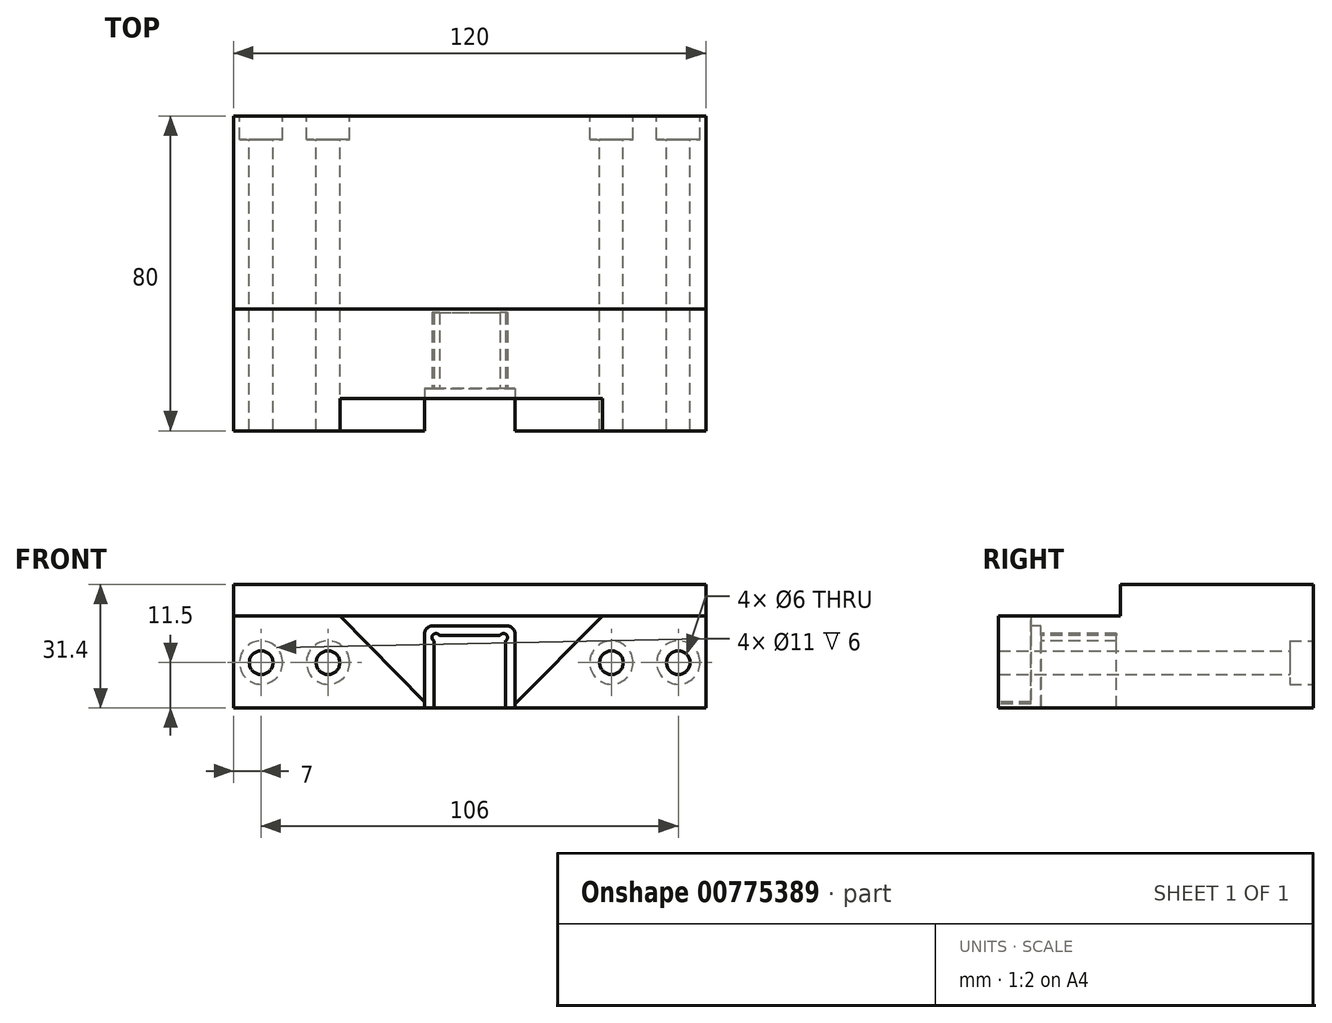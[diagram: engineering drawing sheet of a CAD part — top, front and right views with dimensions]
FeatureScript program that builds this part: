
annotation { "Feature Type Name" : "Feature", "Feature Type Description" : "" }
export const myFeature = defineFeature(function(context is Context, id is Id, definition is map)
    precondition{}
    {
        {
            var Q0;
            Q0=qCreatedBy(makeId("Front.planeOp"),FACE);
            var sketch = newSketch(context, id + "F0", { "sketchPlane" : qUnion([Q0])});
            skLineSegment(sketch, "E0.bottom", {"start": v(-60, 0) * mm, "end": v(60, 0) * mm});
            skLineSegment(sketch, "E0.top", {"start": v(-60, -39.79) * mm, "end": v(60, -39.79) * mm});
            skLineSegment(sketch, "E0.left", {"start": v(-60, 0) * mm, "end": v(-60, -39.79) * mm});
            skLineSegment(sketch, "E0.right", {"start": v(60, 0) * mm, "end": v(60, -39.79) * mm});
            skSolve(sketch);
        }
        {
            var Q0;
            Q0 = qSketchRegion(id + "F0", true);
            extrude(context, id + "F1", {"entities" : qUnion([Q0]), "depth" : 80 * mm, "offsetDistance" : 25 * mm});
        }
        {
            var Q0;
            Q0=makeQuery(id+"F1.opExtrude","CAP_FACE",FACE,{"disambiguationData":[OSD([sQuery(id+"F0.wireOp",EDGE,"E0.bottom"),sQuery(id+"F0.wireOp",EDGE,"E0.top"),sQuery(id+"F0.wireOp",EDGE,"E0.left"),sQuery(id+"F0.wireOp",EDGE,"E0.right")])],"isStart":false});
            var sketch = newSketch(context, id + "F2", { "sketchPlane" : qUnion([Q0])});
            skLineSegment(sketch, "E1.bottom", {"start": v(-9.09, -39.79) * mm, "end": v(9.09, -39.79) * mm});
            skLineSegment(sketch, "E1.top", {"start": v(-9.1, -21.39) * mm, "end": v(9.1, -21.39) * mm});
            skLineSegment(sketch, "E1.left", {"start": v(-9.09, -39.79) * mm, "end": v(-9.1, -21.39) * mm});
            skLineSegment(sketch, "E1.right", {"start": v(9.1, -39.79) * mm, "end": v(9.1, -21.39) * mm});
            skSolve(sketch);
        }
        {
            var Q0;
            Q0 = qSketchRegion(id + "F2", true);
            extrude(context, id + "F3", {"entities" : qUnion([Q0]), "operationType" : NewBodyOperationType.REMOVE, "oppositeDirection" : true, "depth" : 30.03 * mm, "offsetDistance" : 25 * mm});
        }
        {
            var Q0;
            Q0=makeQuery(id+"F1.opExtrude","CAP_FACE",FACE,{"disambiguationData":[OSD([sQuery(id+"F0.wireOp",EDGE,"E0.bottom"),sQuery(id+"F0.wireOp",EDGE,"E0.top"),sQuery(id+"F0.wireOp",EDGE,"E0.left"),sQuery(id+"F0.wireOp",EDGE,"E0.right")])],"isStart":false});
            var sketch = newSketch(context, id + "F4", { "sketchPlane" : qUnion([Q0])});
            skLineSegment(sketch, "E2.bottom", {"start": v(-11.5, -39.79) * mm, "end": v(11.5, -39.79) * mm});
            skLineSegment(sketch, "E2.top", {"start": v(-11.5, -18.99) * mm, "end": v(11.5, -18.99) * mm});
            skLineSegment(sketch, "E2.left", {"start": v(-11.5, -39.79) * mm, "end": v(-11.5, -18.99) * mm});
            skLineSegment(sketch, "E2.right", {"start": v(11.5, -39.79) * mm, "end": v(11.5, -18.99) * mm});
            skSolve(sketch);
        }
        {
            var Q0;
            Q0 = qSketchRegion(id + "F4", true);
            extrude(context, id + "F5", {"entities" : qUnion([Q0]), "operationType" : NewBodyOperationType.REMOVE, "oppositeDirection" : true, "depth" : 10.8 * mm, "offsetDistance" : 25 * mm});
        }
        {
            var Q0;
            Q0=makeQuery(id+"F5.boolean.opBoolean","COPY",FACE,{"derivedFrom":makeQuery(id+"F5.opExtrude","CAP_FACE",FACE,{"disambiguationData":[OSD([sQuery(id+"F4.wireOp",EDGE,"E2.bottom"),sQuery(id+"F4.wireOp",EDGE,"E2.top"),sQuery(id+"F4.wireOp",EDGE,"E2.left"),sQuery(id+"F4.wireOp",EDGE,"E2.right")])],"isStart":false})});
            var sketch = newSketch(context, id + "F6", { "sketchPlane" : qUnion([Q0])});
            skLineSegment(sketch, "E3.0", {"start": v(-9.6, -20.89) * mm, "end": v(-9.59, -39.79) * mm});
            skLineSegment(sketch, "E3.1", {"start": v(9.6, -20.89) * mm, "end": v(-9.6, -20.89) * mm});
            skLineSegment(sketch, "E3.2", {"start": v(9.6, -20.89) * mm, "end": v(9.6, -39.79) * mm});
            skCircle(sketch, "E4", {"center": v(-8.6, -21.89) * mm, "radius": 1 * mm});
            skCircle(sketch, "E5", {"center": v(8.59, -21.89) * mm, "radius": 1 * mm});
            skSolve(sketch);
        }
        {
            var Q0;
            {var subQ0=sQuery(id+"F6.wireOp",EDGE,"E4");var subQ1=makeQuery(id+"F6.imprint","INTERSECT",VERTEX,{"derivedFrom":[sQuery(id+"F6.wireOp",EDGE,"E3.0"),subQ0]});Q0=makeQuery(id+"F6.imprint","IMPRINT",FACE,{"disambiguationData":[TD([[makeQuery(id+"F6.imprint","IMPRINT",EDGE,{"disambiguationData":[TD([[subQ1,1.0]])],"derivedFrom":subQ0}),1.0]])]});}
            var Q1;
            {var subQ4=sQuery(id+"F6.wireOp",EDGE,"E5");var subQ8=makeQuery(id+"F6.imprint","INTERSECT",VERTEX,{"derivedFrom":[sQuery(id+"F6.wireOp",EDGE,"E3.1"),subQ4]});Q1=makeQuery(id+"F6.imprint","IMPRINT",FACE,{"disambiguationData":[TD([[makeQuery(id+"F6.imprint","IMPRINT",EDGE,{"disambiguationData":[TD([[subQ8,1.0]])],"derivedFrom":subQ4}),1.0]])]});}
            var Q2;
            Q2=makeQuery(id+"F3.boolean.opBoolean","COPY",FACE,{"derivedFrom":makeQuery(id+"F3.opExtrude","CAP_FACE",FACE,{"disambiguationData":[OSD([sQuery(id+"F2.wireOp",EDGE,"E1.bottom"),sQuery(id+"F2.wireOp",EDGE,"E1.top"),sQuery(id+"F2.wireOp",EDGE,"E1.left"),sQuery(id+"F2.wireOp",EDGE,"E1.right")])],"isStart":false})});
            extrude(context, id + "F7", {"entities" : qUnion([Q0, Q1]), "operationType" : NewBodyOperationType.REMOVE, "endBound" : BoundingType.UP_TO_SURFACE, "oppositeDirection" : true, "depth" : 25 * mm, "endBoundEntityFace" : qUnion([Q2]), "offsetDistance" : 25 * mm});
        }
        {
            var Q0;
            Q0=makeQuery(id+"F5.boolean.opBoolean","COPY",EDGE,{"derivedFrom":makeQuery(id+"F5.opExtrude","SWEPT_EDGE",EDGE,{"disambiguationData":[OSD([sQuery(id+"F4.wireOp",EDGE,"E2.top"),sQuery(id+"F4.wireOp",EDGE,"E2.left")])]})});
            var Q1;
            Q1=makeQuery(id+"F5.boolean.opBoolean","COPY",EDGE,{"derivedFrom":makeQuery(id+"F5.opExtrude","SWEPT_EDGE",EDGE,{"disambiguationData":[OSD([sQuery(id+"F4.wireOp",EDGE,"E2.top"),sQuery(id+"F4.wireOp",EDGE,"E2.right")])]})});
            fillet(context, id + "F8", {"entities" : qUnion([Q0, Q1]), "radius" : 2 * mm, "tangentPropagation" : true, "allowEdgeOverflow" : false});
        }
        {
            var Q0;
            Q0=makeQuery(id+"F1.opExtrude","CAP_FACE",FACE,{"disambiguationData":[OSD([sQuery(id+"F0.wireOp",EDGE,"E0.bottom"),sQuery(id+"F0.wireOp",EDGE,"E0.top"),sQuery(id+"F0.wireOp",EDGE,"E0.left"),sQuery(id+"F0.wireOp",EDGE,"E0.right")])],"isStart":false});
            var sketch = newSketch(context, id + "F9", { "sketchPlane" : qUnion([Q0])});
            skLineSegment(sketch, "E6", {"start": v(-49, 0) * mm, "end": v(0.2, -50.24) * mm});
            skLineSegment(sketch, "E7", {"start": v(0.2, -50.24) * mm, "end": v(49.92, 0) * mm});
            skLineSegment(sketch, "E8", {"start": v(0.2, -50.24) * mm, "end": v(0.2, 6.07) * mm});
            skLineSegment(sketch, "E9", {"start": v(-12.95, -39.79) * mm, "end": v(13.39, -39.79) * mm});
            skPoint(sketch, "E10", {"position": v(-10.03, -39.79) * mm});
            skPoint(sketch, "E11", {"position": v(10.54, -39.79) * mm});
            skSolve(sketch);
        }
        {
            var Q0;
            {var subQ0=sQuery(id+"F9.wireOp",EDGE,"E6");var subQ1=sQuery(id+"F0.wireOp",EDGE,"E0.bottom");var subQ2=makeQuery(id+"F1.opExtrude","CAP_EDGE",EDGE,{"disambiguationData":[OSD([subQ1])],"isStart":false});var subQ3=makeQuery(id+"F9.imprint","INTERSECT",VERTEX,{"derivedFrom":[subQ2,subQ0]});Q0=makeQuery(id+"F9.imprint","IMPRINT",FACE,{"disambiguationData":[TD([[makeQuery(id+"F9.imprint","IMPRINT",EDGE,{"disambiguationData":[TD([[subQ3,-1.0]])],"derivedFrom":subQ0}),1.0]])]});}
            var Q1;
            {var subQ0=sQuery(id+"F0.wireOp",EDGE,"E0.bottom");var subQ4=sQuery(id+"F9.wireOp",EDGE,"E7");var subQ5=makeQuery(id+"F1.opExtrude","CAP_EDGE",EDGE,{"disambiguationData":[OSD([subQ0])],"isStart":false});var subQ6=makeQuery(id+"F9.imprint","INTERSECT",VERTEX,{"derivedFrom":[subQ5,subQ4]});Q1=makeQuery(id+"F9.imprint","IMPRINT",FACE,{"disambiguationData":[TD([[makeQuery(id+"F9.imprint","IMPRINT",EDGE,{"disambiguationData":[TD([[subQ6,1.0]])],"derivedFrom":subQ4}),1.0]])]});}
            extrude(context, id + "F10", {"entities" : qUnion([Q0, Q1]), "operationType" : NewBodyOperationType.REMOVE, "oppositeDirection" : true, "depth" : 8.25 * mm, "offsetDistance" : 25 * mm});
        }
        {
            var Q0;
            Q0=makeQuery(id+"F1.opExtrude","SWEPT_FACE",FACE,{"disambiguationData":[OSD([sQuery(id+"F0.wireOp",EDGE,"E0.right")])]});
            var sketch = newSketch(context, id + "F11", { "sketchPlane" : qUnion([Q0])});
            skLineSegment(sketch, "E12", {"start": v(0, -8.4) * mm, "end": v(-49, -8.4) * mm});
            skLineSegment(sketch, "E13", {"start": v(-49, -8.4) * mm, "end": v(-49, -16.39) * mm});
            skLineSegment(sketch, "E14", {"start": v(-49, -16.39) * mm, "end": v(-80, -16.4) * mm});
            skSolve(sketch);
        }
        {
            var Q0;
            {var subQ3=sQuery(id+"F11.wireOp",EDGE,"E12");Q0=makeQuery(id+"F11.imprint","IMPRINT",FACE,{"disambiguationData":[TD([[makeQuery(id+"F11.imprint","IMPRINT",EDGE,{"derivedFrom":subQ3}),-1.0]])]});}
            extrude(context, id + "F12", {"entities" : qUnion([Q0]), "operationType" : NewBodyOperationType.REMOVE, "endBound" : BoundingType.THROUGH_ALL, "oppositeDirection" : true, "depth" : 25 * mm, "offsetDistance" : 25 * mm});
        }
        {
            var Q0;
            Q0=makeQuery(id+"F1.opExtrude","CAP_FACE",FACE,{"disambiguationData":[OSD([sQuery(id+"F0.wireOp",EDGE,"E0.bottom"),sQuery(id+"F0.wireOp",EDGE,"E0.top"),sQuery(id+"F0.wireOp",EDGE,"E0.left"),sQuery(id+"F0.wireOp",EDGE,"E0.right")])],"isStart":true});
            var sketch = newSketch(context, id + "F13", { "sketchPlane" : qUnion([Q0])});
            skLineSegment(sketch, "E15", {"start": v(-60, -28.29) * mm, "end": v(60, -28.29) * mm, "construction": true});
            skLineSegment(sketch, "E16", {"start": v(-36, -20.66) * mm, "end": v(-36, -35.92) * mm, "construction": true});
            skLineSegment(sketch, "E17", {"start": v(-53, -20.66) * mm, "end": v(-53, -35.92) * mm, "construction": true});
            skLineSegment(sketch, "E18", {"start": v(36, -20.66) * mm, "end": v(36, -35.92) * mm, "construction": true});
            skLineSegment(sketch, "E19", {"start": v(53, -20.66) * mm, "end": v(53, -35.92) * mm, "construction": true});
            skCircle(sketch, "E20", {"center": v(-53, -28.29) * mm, "radius": 3 * mm});
            skCircle(sketch, "E21", {"center": v(-36, -28.29) * mm, "radius": 3 * mm});
            skCircle(sketch, "E22", {"center": v(36, -28.29) * mm, "radius": 3 * mm});
            skCircle(sketch, "E23", {"center": v(53, -28.29) * mm, "radius": 3 * mm});
            skSolve(sketch);
        }
        {
            var Q0;
            Q0=makeQuery(id+"F13.imprint","IMPRINT",FACE,{"disambiguationData":[TD([[makeQuery(id+"F13.imprint","IMPRINT",EDGE,{"derivedFrom":sQuery(id+"F13.wireOp",EDGE,"E20")}),1.0]])]});
            var Q1;
            Q1=makeQuery(id+"F13.imprint","IMPRINT",FACE,{"disambiguationData":[TD([[makeQuery(id+"F13.imprint","IMPRINT",EDGE,{"derivedFrom":sQuery(id+"F13.wireOp",EDGE,"E21")}),1.0]])]});
            var Q2;
            Q2=makeQuery(id+"F13.imprint","IMPRINT",FACE,{"disambiguationData":[TD([[makeQuery(id+"F13.imprint","IMPRINT",EDGE,{"derivedFrom":sQuery(id+"F13.wireOp",EDGE,"E22")}),1.0]])]});
            var Q3;
            Q3=makeQuery(id+"F13.imprint","IMPRINT",FACE,{"disambiguationData":[TD([[makeQuery(id+"F13.imprint","IMPRINT",EDGE,{"derivedFrom":sQuery(id+"F13.wireOp",EDGE,"E23")}),1.0]])]});
            extrude(context, id + "F14", {"entities" : qUnion([Q0, Q1, Q2, Q3]), "operationType" : NewBodyOperationType.REMOVE, "endBound" : BoundingType.THROUGH_ALL, "oppositeDirection" : true, "depth" : 25 * mm, "offsetDistance" : 25 * mm});
        }
        {
            var Q0;
            Q0=makeQuery(id+"F1.opExtrude","CAP_FACE",FACE,{"disambiguationData":[OSD([sQuery(id+"F0.wireOp",EDGE,"E0.bottom"),sQuery(id+"F0.wireOp",EDGE,"E0.top"),sQuery(id+"F0.wireOp",EDGE,"E0.left"),sQuery(id+"F0.wireOp",EDGE,"E0.right")])],"isStart":true});
            var sketch = newSketch(context, id + "F15", { "sketchPlane" : qUnion([Q0])});
            skCircle(sketch, "E24", {"center": v(-53, -28.29) * mm, "radius": 5.5 * mm});
            skCircle(sketch, "E25", {"center": v(-36, -28.29) * mm, "radius": 5.5 * mm});
            skCircle(sketch, "E26", {"center": v(36, -28.29) * mm, "radius": 5.5 * mm});
            skCircle(sketch, "E27", {"center": v(53, -28.29) * mm, "radius": 5.5 * mm});
            skSolve(sketch);
        }
        {
            var Q0;
            Q0=makeQuery(id+"F15.imprint","IMPRINT",FACE,{"disambiguationData":[TD([[makeQuery(id+"F15.imprint","IMPRINT",EDGE,{"derivedFrom":sQuery(id+"F15.wireOp",EDGE,"E24")}),1.0]])]});
            var Q1;
            Q1=makeQuery(id+"F15.imprint","IMPRINT",FACE,{"disambiguationData":[TD([[makeQuery(id+"F15.imprint","IMPRINT",EDGE,{"derivedFrom":sQuery(id+"F15.wireOp",EDGE,"E25")}),1.0]])]});
            var Q2;
            Q2=makeQuery(id+"F15.imprint","IMPRINT",FACE,{"disambiguationData":[TD([[makeQuery(id+"F15.imprint","IMPRINT",EDGE,{"derivedFrom":sQuery(id+"F15.wireOp",EDGE,"E26")}),1.0]])]});
            var Q3;
            Q3=makeQuery(id+"F15.imprint","IMPRINT",FACE,{"disambiguationData":[TD([[makeQuery(id+"F15.imprint","IMPRINT",EDGE,{"derivedFrom":sQuery(id+"F15.wireOp",EDGE,"E27")}),1.0]])]});
            extrude(context, id + "F16", {"entities" : qUnion([Q0, Q1, Q2, Q3]), "operationType" : NewBodyOperationType.REMOVE, "oppositeDirection" : true, "depth" : 6 * mm, "offsetDistance" : 25 * mm});
        }
    });
